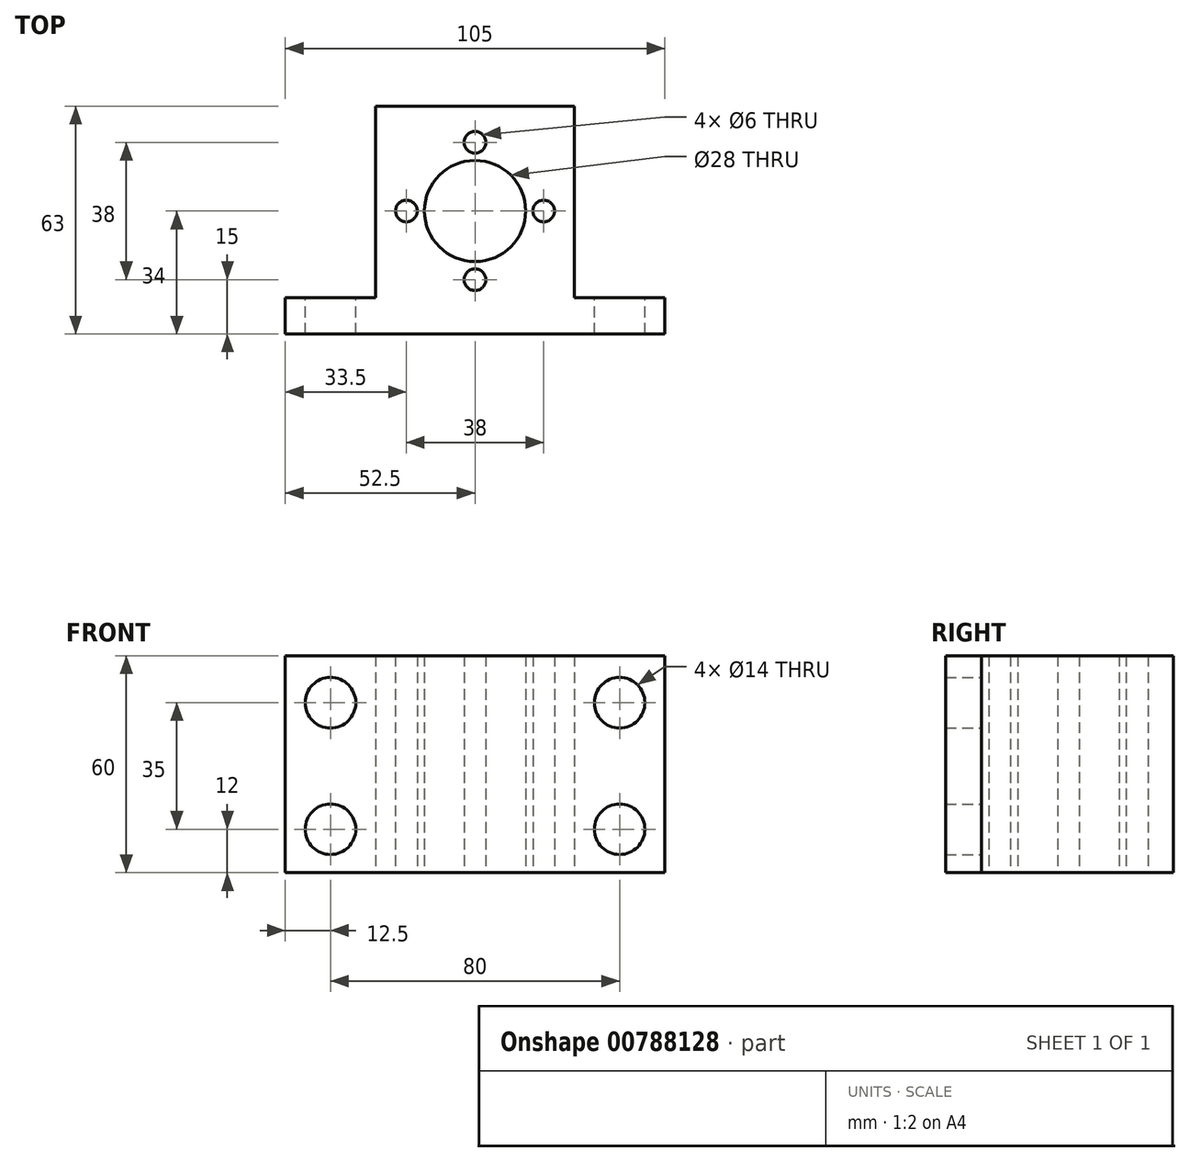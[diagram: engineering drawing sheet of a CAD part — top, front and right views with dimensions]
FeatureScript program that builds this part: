
annotation { "Feature Type Name" : "Feature", "Feature Type Description" : "" }
export const myFeature = defineFeature(function(context is Context, id is Id, definition is map)
    precondition{}
    {
        {
            var Q0;
            Q0=qCreatedBy(makeId("Top.planeOp"),FACE);
            var sketch = newSketch(context, id + "F0", { "sketchPlane" : qUnion([Q0])});
            skLineSegment(sketch, "E0", {"start": v(-52.5, 0) * mm, "end": v(-52.5, 10) * mm});
            skLineSegment(sketch, "E1", {"start": v(-52.5, 10) * mm, "end": v(-27.5, 10) * mm});
            skLineSegment(sketch, "E2", {"start": v(-27.5, 10) * mm, "end": v(-27.5, 63) * mm});
            skLineSegment(sketch, "E3", {"start": v(-27.5, 63) * mm, "end": v(27.5, 63) * mm});
            skLineSegment(sketch, "E4", {"start": v(27.5, 63) * mm, "end": v(27.5, 10) * mm});
            skLineSegment(sketch, "E5", {"start": v(27.5, 10) * mm, "end": v(52.5, 10) * mm});
            skLineSegment(sketch, "E6", {"start": v(52.5, 10) * mm, "end": v(52.5, 0) * mm});
            skLineSegment(sketch, "E7", {"start": v(52.5, 0) * mm, "end": v(-52.5, 0) * mm});
            skPoint(sketch, "E8", {"position": v(0, 0) * mm});
            skPoint(sketch, "E9", {"position": v(-40, 10) * mm});
            skPoint(sketch, "E10", {"position": v(40, 10) * mm});
            skCircle(sketch, "E11", {"center": v(0, 34) * mm, "radius": 14 * mm});
            skCircle(sketch, "E12", {"center": v(0, 53) * mm, "radius": 3 * mm});
            skCircle(sketch, "E13", {"center": v(0, 15) * mm, "radius": 3 * mm});
            skCircle(sketch, "E14", {"center": v(19, 34) * mm, "radius": 3 * mm});
            skCircle(sketch, "E15", {"center": v(-19, 34) * mm, "radius": 3 * mm});
            skSolve(sketch);
        }
        {
            var Q0;
            Q0=qSketchRegion(id+"F0",true);
            extrude(context, id + "F1", {"entities" : qUnion([Q0]), "depth" : 60 * mm, "offsetDistance" : 25 * mm});
        }
        {
            var Q0;
            Q0=makeQuery(id+"F1.opExtrude","SWEPT_FACE",FACE,{"disambiguationData":[OSD([sQuery(id+"F0.wireOp",EDGE,"E5")])]});
            var sketch = newSketch(context, id + "F2", { "sketchPlane" : qUnion([Q0])});
            skCircle(sketch, "E16", {"center": v(-40, 47) * mm, "radius": 7 * mm});
            skCircle(sketch, "E17", {"center": v(-40, 12) * mm, "radius": 7 * mm});
            skCircle(sketch, "E18", {"center": v(40, 47) * mm, "radius": 7 * mm});
            skCircle(sketch, "E19", {"center": v(40, 12) * mm, "radius": 7 * mm});
            skSolve(sketch);
        }
        {
            var Q0;
            Q0=qSketchRegion(id+"F2",true);
            extrude(context, id + "F3", {"entities" : qUnion([Q0]), "operationType" : NewBodyOperationType.REMOVE, "oppositeDirection" : true, "depth" : 25 * mm, "offsetDistance" : 25 * mm});
        }
    });
